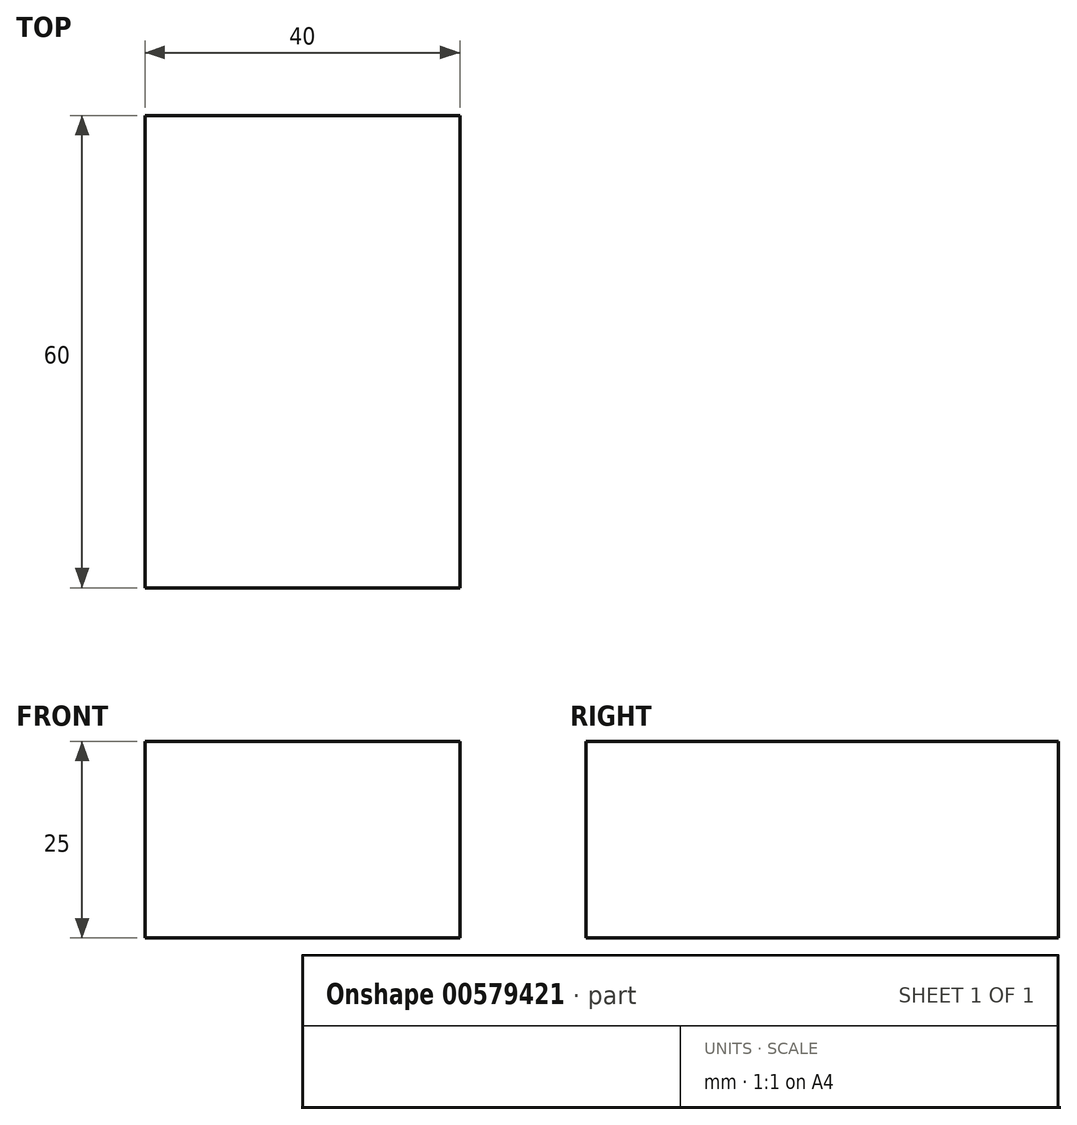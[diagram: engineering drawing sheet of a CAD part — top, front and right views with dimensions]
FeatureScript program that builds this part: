
annotation { "Feature Type Name" : "Feature", "Feature Type Description" : "" }
export const myFeature = defineFeature(function(context is Context, id is Id, definition is map)
    precondition{}
    {
        {
            var Q0;
            Q0=qCreatedBy(makeId("Top.planeOp"),FACE);
            var sketch = newSketch(context, id + "F0", { "sketchPlane" : qUnion([Q0])});
            skPoint(sketch, "E0.middle", {"position": v(0, 0) * mm});
            skLineSegment(sketch, "E1.bottom", {"start": v(0, 0) * mm, "end": v(40, 0) * mm});
            skLineSegment(sketch, "E1.top", {"start": v(0, 60) * mm, "end": v(40, 60) * mm});
            skLineSegment(sketch, "E1.left", {"start": v(0, 0) * mm, "end": v(0, 60) * mm});
            skLineSegment(sketch, "E1.right", {"start": v(40, 0) * mm, "end": v(40, 60) * mm});
            skSolve(sketch);
        }
        {
            var Q0;
            Q0 = qSketchRegion(id + "F0", true);
            extrude(context, id + "F1", {"entities" : qUnion([Q0]), "depth" : 25 * mm, "offsetDistance" : 25 * mm});
        }
    });
